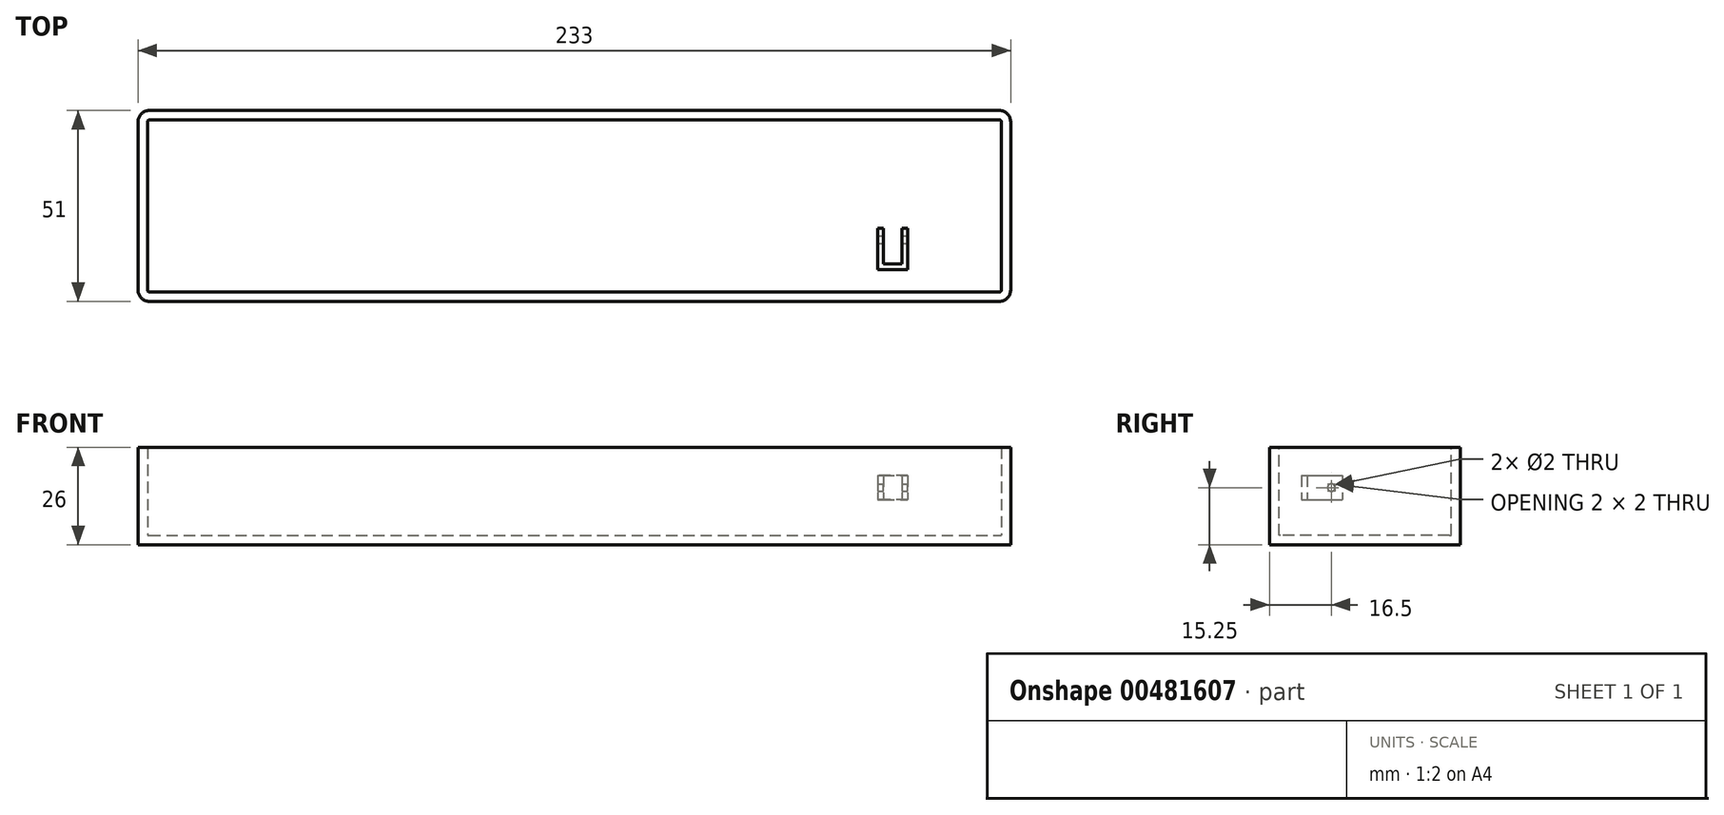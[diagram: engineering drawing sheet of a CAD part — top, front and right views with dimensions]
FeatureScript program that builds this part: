
annotation { "Feature Type Name" : "Feature", "Feature Type Description" : "" }
export const myFeature = defineFeature(function(context is Context, id is Id, definition is map)
    precondition{}
    {
        {
            var Q0;
            Q0=qCreatedBy(makeId("Top.planeOp"),FACE);
            var sketch = newSketch(context, id + "F0", { "sketchPlane" : qUnion([Q0])});
            skLineSegment(sketch, "E0.bottom", {"start": v(-116.5, 25.5) * mm, "end": v(116.5, 25.5) * mm});
            skLineSegment(sketch, "E0.top", {"start": v(-116.5, -25.5) * mm, "end": v(116.5, -25.5) * mm});
            skLineSegment(sketch, "E0.left", {"start": v(-116.5, 25.5) * mm, "end": v(-116.5, -25.5) * mm});
            skLineSegment(sketch, "E0.right", {"start": v(116.5, 25.5) * mm, "end": v(116.5, -25.5) * mm});
            skPoint(sketch, "E0.middle", {"position": v(0, 0) * mm});
            skSolve(sketch);
        }
        {
            var Q0;
            Q0 = qSketchRegion(id + "F0", true);
            extrude(context, id + "F1", {"entities" : qUnion([Q0]), "depth" : 26 * mm});
        }
        {
            var Q0;
            Q0=makeQuery(id+"F1.opExtrude","SWEPT_EDGE",EDGE,{"disambiguationData":[OSD([sQuery(id+"F0.wireOp",EDGE,"E0.top"),sQuery(id+"F0.wireOp",EDGE,"E0.left")])]});
            var Q1;
            Q1=makeQuery(id+"F1.opExtrude","SWEPT_EDGE",EDGE,{"disambiguationData":[OSD([sQuery(id+"F0.wireOp",EDGE,"E0.top"),sQuery(id+"F0.wireOp",EDGE,"E0.right")])]});
            var Q2;
            Q2=makeQuery(id+"F1.opExtrude","SWEPT_EDGE",EDGE,{"disambiguationData":[OSD([sQuery(id+"F0.wireOp",EDGE,"E0.bottom"),sQuery(id+"F0.wireOp",EDGE,"E0.right")])]});
            var Q3;
            Q3=makeQuery(id+"F1.opExtrude","SWEPT_EDGE",EDGE,{"disambiguationData":[OSD([sQuery(id+"F0.wireOp",EDGE,"E0.bottom"),sQuery(id+"F0.wireOp",EDGE,"E0.left")])]});
            fillet(context, id + "F2", {"entities" : qUnion([Q0, Q1, Q2, Q3]), "radius" : 3 * mm, "tangentPropagation" : true, "allowEdgeOverflow" : false});
        }
        {
            var Q0;
            Q0=makeQuery(id+"F1.opExtrude","CAP_FACE",FACE,{"disambiguationData":[OSD([sQuery(id+"F0.wireOp",EDGE,"E0.bottom"),sQuery(id+"F0.wireOp",EDGE,"E0.top"),sQuery(id+"F0.wireOp",EDGE,"E0.left"),sQuery(id+"F0.wireOp",EDGE,"E0.right")])],"isStart":false});
            shell(context, id + "F3", {"entities" : qUnion([Q0]), "thickness" : 2.5 * mm});
        }
        {
            var Q0;
            Q0=makeQuery(id+"F3.opShell","OFFSET_FACE",FACE,{"disambiguationData":[OSD([sQuery(id+"F0.wireOp",EDGE,"E0.bottom"),sQuery(id+"F0.wireOp",EDGE,"E0.top"),sQuery(id+"F0.wireOp",EDGE,"E0.left"),sQuery(id+"F0.wireOp",EDGE,"E0.right")])]});
            var sketch = newSketch(context, id + "F4", { "sketchPlane" : qUnion([Q0])});
            skLineSegment(sketch, "E1", {"start": v(81, -6) * mm, "end": v(82.5, -6) * mm});
            skLineSegment(sketch, "E2", {"start": v(82.5, -6) * mm, "end": v(82.5, -15.5) * mm});
            skLineSegment(sketch, "E3", {"start": v(82.5, -15.5) * mm, "end": v(87.5, -15.5) * mm});
            skLineSegment(sketch, "E4", {"start": v(87.5, -15.5) * mm, "end": v(87.5, -6) * mm});
            skLineSegment(sketch, "E5", {"start": v(87.5, -6) * mm, "end": v(89, -6) * mm});
            skLineSegment(sketch, "E6", {"start": v(89, -6) * mm, "end": v(89, -17) * mm});
            skLineSegment(sketch, "E7", {"start": v(89, -17) * mm, "end": v(81, -17) * mm});
            skLineSegment(sketch, "E8", {"start": v(81, -17) * mm, "end": v(81, -6) * mm});
            skSolve(sketch);
        }
        {
            var Q0;
            Q0=makeQuery(id+"F4.imprint","IMPRINT",FACE,{"disambiguationData":[TD([[makeQuery(id+"F4.imprint","IMPRINT",EDGE,{"derivedFrom":sQuery(id+"F4.wireOp",EDGE,"E1")}),1.0]])]});
            cPlane(context, id + "F5", {"entities" : qUnion([Q0]), "cplaneType" : CPlaneType.OFFSET, "offset" : 9.5 * mm, "width" : 150 * mm, "height" : 150 * mm});
        }
        {
            var Q0;
            Q0=qCreatedBy(id+"F5.planeOp",FACE);
            var sketch = newSketch(context, id + "F6", { "sketchPlane" : qUnion([Q0])});
            skLineSegment(sketch, "E9.0", {"start": v(87.5, -15.5) * mm, "end": v(87.5, -6) * mm});
            skLineSegment(sketch, "E9.1", {"start": v(82.5, -15.5) * mm, "end": v(87.5, -15.5) * mm});
            skLineSegment(sketch, "E9.2", {"start": v(87.5, -6) * mm, "end": v(89, -6) * mm});
            skLineSegment(sketch, "E9.3", {"start": v(82.5, -6) * mm, "end": v(82.5, -15.5) * mm});
            skLineSegment(sketch, "E9.4", {"start": v(89, -6) * mm, "end": v(89, -17) * mm});
            skLineSegment(sketch, "E9.5", {"start": v(89, -17) * mm, "end": v(81, -17) * mm});
            skLineSegment(sketch, "E9.6", {"start": v(81, -17) * mm, "end": v(81, -6) * mm});
            skLineSegment(sketch, "E9.7", {"start": v(81, -6) * mm, "end": v(82.5, -6) * mm});
            skSolve(sketch);
        }
        {
            var Q0;
            Q0 = qSketchRegion(id + "F6", true);
            extrude(context, id + "F7", {"entities" : qUnion([Q0]), "depth" : 6.5 * mm});
        }
        {
            var Q0;
            Q0=makeQuery(id+"F7.opExtrude","SWEPT_FACE",FACE,{"disambiguationData":[OSD([sQuery(id+"F6.wireOp",EDGE,"E9.4")])]});
            var sketch = newSketch(context, id + "F8", { "sketchPlane" : qUnion([Q0])});
            skCircle(sketch, "E10", {"center": v(-9, 15.25) * mm, "radius": 1 * mm});
            skPoint(sketch, "E10.centerSnap0", {"position": v(-6, 15.25) * mm});
            skSolve(sketch);
        }
        {
            var Q0;
            Q0 = qSketchRegion(id + "F8", true);
            extrude(context, id + "F9", {"entities" : qUnion([Q0]), "operationType" : NewBodyOperationType.REMOVE, "oppositeDirection" : true, "depth" : 25 * mm});
        }
    });
